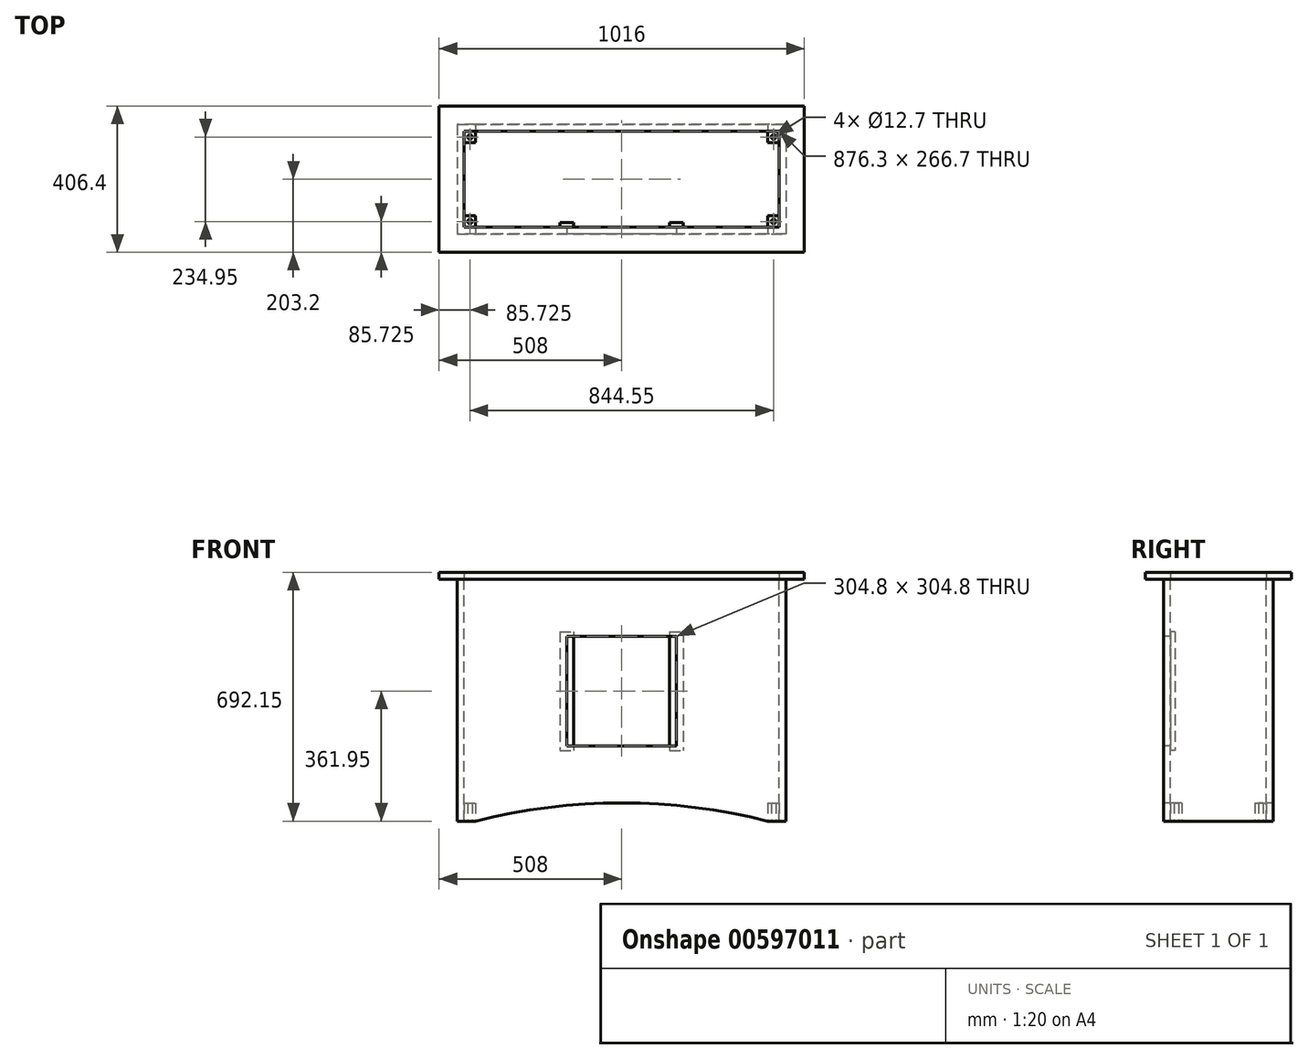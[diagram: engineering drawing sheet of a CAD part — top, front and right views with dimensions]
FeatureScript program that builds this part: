
annotation { "Feature Type Name" : "Feature", "Feature Type Description" : "" }
export const myFeature = defineFeature(function(context is Context, id is Id, definition is map)
    precondition{}
    {
        {
            var Q0;
            Q0=qCreatedBy(makeId("Front.planeOp"),FACE);
            var sketch = newSketch(context, id + "F0", { "sketchPlane" : qUnion([Q0])});
            skLineSegment(sketch, "E0", {"start": v(-406.4, -336.55) * mm, "end": v(-457.2, -336.55) * mm});
            skLineSegment(sketch, "E1", {"start": v(-457.2, -336.55) * mm, "end": v(-457.2, 336.55) * mm});
            skLineSegment(sketch, "E2", {"start": v(-457.2, 336.55) * mm, "end": v(457.2, 336.55) * mm});
            skLineSegment(sketch, "E3", {"start": v(457.2, 336.55) * mm, "end": v(457.2, -336.55) * mm});
            skLineSegment(sketch, "E4", {"start": v(457.2, -336.55) * mm, "end": v(406.4, -336.55) * mm});
            skLineSegment(sketch, "E5", {"start": v(0, 336.55) * mm, "end": v(0, -336.55) * mm, "construction": true});
            skArc(sketch, "E6", {"start": v(406.4, -336.55) * mm, "mid": v(0, -285.75) * mm, "end": v(-406.4, -336.55) * mm});
            skSolve(sketch);
        }
        {
            var Q0;
            Q0 = qSketchRegion(id + "F0", true);
            extrude(context, id + "F1", {"entities" : qUnion([Q0]), "oppositeDirection" : true, "depth" : 304.8 * mm, "offsetDistance" : 25.4 * mm});
        }
        {
            var Q0;
            Q0=makeQuery(id+"F1.opExtrude","SWEPT_FACE",FACE,{"disambiguationData":[OSD([sQuery(id+"F0.wireOp",EDGE,"E2")])]});
            var sketch = newSketch(context, id + "F2", { "sketchPlane" : qUnion([Q0])});
            skLineSegment(sketch, "E7.0", {"start": v(-438.15, 19.05) * mm, "end": v(438.15, 19.05) * mm});
            skLineSegment(sketch, "E7.1", {"start": v(-438.15, 285.75) * mm, "end": v(-438.15, 19.05) * mm});
            skLineSegment(sketch, "E7.2", {"start": v(438.15, 285.75) * mm, "end": v(-438.15, 285.75) * mm});
            skLineSegment(sketch, "E7.3", {"start": v(438.15, 19.05) * mm, "end": v(438.15, 285.75) * mm});
            skSolve(sketch);
        }
        {
            var Q0;
            Q0 = qSketchRegion(id + "F2", true);
            extrude(context, id + "F3", {"entities" : qUnion([Q0]), "operationType" : NewBodyOperationType.REMOVE, "endBound" : BoundingType.THROUGH_ALL, "oppositeDirection" : true, "depth" : 25.4 * mm, "offsetDistance" : 25.4 * mm});
        }
        {
            var Q0;
            Q0=makeQuery(id+"F1.opExtrude","CAP_FACE",FACE,{"disambiguationData":[OSD([sQuery(id+"F0.wireOp",EDGE,"E0"),sQuery(id+"F0.wireOp",EDGE,"E1"),sQuery(id+"F0.wireOp",EDGE,"E2"),sQuery(id+"F0.wireOp",EDGE,"E3"),sQuery(id+"F0.wireOp",EDGE,"E4"),sQuery(id+"F0.wireOp",EDGE,"E6")])],"isStart":true});
            var sketch = newSketch(context, id + "F4", { "sketchPlane" : qUnion([Q0])});
            skLineSegment(sketch, "E8", {"start": v(0, 336.55) * mm, "end": v(0, -285.75) * mm});
            skLineSegment(sketch, "E9.bottom", {"start": v(152.4, 177.8) * mm, "end": v(-152.4, 177.8) * mm});
            skLineSegment(sketch, "E9.top", {"start": v(152.4, -127) * mm, "end": v(-152.4, -127) * mm});
            skLineSegment(sketch, "E9.left", {"start": v(152.4, 177.8) * mm, "end": v(152.4, -127) * mm});
            skLineSegment(sketch, "E9.right", {"start": v(-152.4, 177.8) * mm, "end": v(-152.4, -127) * mm});
            skPoint(sketch, "E9.middle", {"position": v(0, 25.4) * mm});
            skSolve(sketch);
        }
        {
            var Q0;
            Q0 = qSketchRegion(id + "F4", true);
            extrude(context, id + "F5", {"entities" : qUnion([Q0]), "operationType" : NewBodyOperationType.REMOVE, "oppositeDirection" : true, "depth" : 25.4 * mm, "offsetDistance" : 25.4 * mm});
        }
        {
            var Q0;
            Q0=makeQuery(id+"F3.boolean.opBoolean","COPY",FACE,{"derivedFrom":makeQuery(id+"F3.opExtrude","SWEPT_FACE",FACE,{"disambiguationData":[OSD([sQuery(id+"F2.wireOp",EDGE,"E7.0")])]})});
            var sketch = newSketch(context, id + "F6", { "sketchPlane" : qUnion([Q0])});
            skLineSegment(sketch, "E10.bottom", {"start": v(171.25, 190.5) * mm, "end": v(133.15, 190.5) * mm});
            skLineSegment(sketch, "E10.top", {"start": v(171.25, -139.7) * mm, "end": v(133.15, -139.7) * mm});
            skLineSegment(sketch, "E10.left", {"start": v(171.25, 190.5) * mm, "end": v(171.25, -139.7) * mm});
            skLineSegment(sketch, "E10.right", {"start": v(133.15, 190.5) * mm, "end": v(133.15, -139.7) * mm});
            skLineSegment(sketch, "E11.bottom", {"start": v(-133.35, 190.5) * mm, "end": v(-171.45, 190.5) * mm});
            skLineSegment(sketch, "E11.top", {"start": v(-133.35, -139.7) * mm, "end": v(-171.45, -139.7) * mm});
            skLineSegment(sketch, "E11.left", {"start": v(-133.35, 190.5) * mm, "end": v(-133.35, -139.7) * mm});
            skLineSegment(sketch, "E11.right", {"start": v(-171.45, 190.5) * mm, "end": v(-171.45, -139.7) * mm});
            skSolve(sketch);
        }
        {
            var Q0;
            Q0 = qSketchRegion(id + "F6", true);
            extrude(context, id + "F7", {"entities" : qUnion([Q0]), "depth" : 12.7 * mm, "offsetDistance" : 25.4 * mm});
        }
        {
            var Q0;
            Q0=makeQuery(id+"F1.opExtrude","SWEPT_FACE",FACE,{"disambiguationData":[OSD([sQuery(id+"F0.wireOp",EDGE,"E2")])]});
            var sketch = newSketch(context, id + "F8", { "sketchPlane" : qUnion([Q0])});
            skLineSegment(sketch, "E12.bottom", {"start": v(-508, 355.6) * mm, "end": v(508, 355.6) * mm});
            skLineSegment(sketch, "E12.top", {"start": v(-508, -50.8) * mm, "end": v(508, -50.8) * mm});
            skLineSegment(sketch, "E12.left", {"start": v(-508, 355.6) * mm, "end": v(-508, -50.8) * mm});
            skLineSegment(sketch, "E12.right", {"start": v(508, 355.6) * mm, "end": v(508, -50.8) * mm});
            skPoint(sketch, "E12.middle", {"position": v(0, 152.4) * mm});
            skPoint(sketch, "E12.middle.positionSnap0", {"position": v(-438.15, 152.4) * mm});
            skPoint(sketch, "E12.middle.positionSnap1", {"position": v(0, 285.75) * mm});
            skPoint(sketch, "E12.centerSnap0", {"position": v(-438.15, 152.4) * mm});
            skPoint(sketch, "E12.centerSnap1", {"position": v(0, 285.75) * mm});
            skLineSegment(sketch, "E13.0", {"start": v(-438.15, 285.75) * mm, "end": v(-438.15, 19.05) * mm});
            skLineSegment(sketch, "E13.1", {"start": v(438.15, 285.75) * mm, "end": v(-438.15, 285.75) * mm});
            skLineSegment(sketch, "E13.2", {"start": v(438.15, 19.05) * mm, "end": v(438.15, 285.75) * mm});
            skLineSegment(sketch, "E13.3", {"start": v(-438.15, 19.05) * mm, "end": v(438.15, 19.05) * mm});
            skSolve(sketch);
        }
        {
            var Q0;
            Q0 = qSketchRegion(id + "F8", true);
            extrude(context, id + "F9", {"entities" : qUnion([Q0]), "depth" : 19.05 * mm, "offsetDistance" : 25.4 * mm});
        }
        {
            var Q0;
            Q0=makeQuery(id+"F1.opExtrude","SWEPT_FACE",FACE,{"disambiguationData":[OSD([sQuery(id+"F0.wireOp",EDGE,"E0")])]});
            var sketch = newSketch(context, id + "F10", { "sketchPlane" : qUnion([Q0])});
            skLineSegment(sketch, "E14.bottom", {"start": v(-438.15, -19.05) * mm, "end": v(-406.4, -19.05) * mm});
            skLineSegment(sketch, "E14.top", {"start": v(-438.15, -50.8) * mm, "end": v(-406.4, -50.8) * mm});
            skLineSegment(sketch, "E14.left", {"start": v(-438.15, -19.05) * mm, "end": v(-438.15, -50.8) * mm});
            skLineSegment(sketch, "E14.right", {"start": v(-406.4, -19.05) * mm, "end": v(-406.4, -50.8) * mm});
            skLineSegment(sketch, "E15.bottom", {"start": v(-438.15, -285.75) * mm, "end": v(-406.4, -285.75) * mm});
            skLineSegment(sketch, "E15.top", {"start": v(-438.15, -254) * mm, "end": v(-406.4, -254) * mm});
            skLineSegment(sketch, "E15.left", {"start": v(-438.15, -285.75) * mm, "end": v(-438.15, -254) * mm});
            skLineSegment(sketch, "E15.right", {"start": v(-406.4, -285.75) * mm, "end": v(-406.4, -254) * mm});
            skLineSegment(sketch, "E16.bottom", {"start": v(438.15, -19.05) * mm, "end": v(406.4, -19.05) * mm});
            skLineSegment(sketch, "E16.top", {"start": v(438.15, -50.8) * mm, "end": v(406.4, -50.8) * mm});
            skLineSegment(sketch, "E16.left", {"start": v(438.15, -19.05) * mm, "end": v(438.15, -50.8) * mm});
            skLineSegment(sketch, "E16.right", {"start": v(406.4, -19.05) * mm, "end": v(406.4, -50.8) * mm});
            skLineSegment(sketch, "E17.bottom", {"start": v(406.4, -254) * mm, "end": v(438.15, -254) * mm});
            skLineSegment(sketch, "E17.top", {"start": v(406.4, -285.75) * mm, "end": v(438.15, -285.75) * mm});
            skLineSegment(sketch, "E17.left", {"start": v(406.4, -254) * mm, "end": v(406.4, -285.75) * mm});
            skLineSegment(sketch, "E17.right", {"start": v(438.15, -254) * mm, "end": v(438.15, -285.75) * mm});
            skCircle(sketch, "E18", {"center": v(-422.28, -34.92) * mm, "radius": 6.35 * mm});
            skPoint(sketch, "E18.centerSnap0", {"position": v(-438.15, -34.92) * mm});
            skPoint(sketch, "E18.centerSnap1", {"position": v(-422.28, -50.8) * mm});
            skCircle(sketch, "E19", {"center": v(-422.28, -269.88) * mm, "radius": 6.35 * mm});
            skLineSegment(sketch, "E20", {"start": v(-438.15, -254) * mm, "end": v(-406.4, -285.75) * mm, "construction": true});
            skCircle(sketch, "E21", {"center": v(422.28, -269.88) * mm, "radius": 6.35 * mm});
            skPoint(sketch, "E21.centerSnap0", {"position": v(406.4, -269.88) * mm});
            skPoint(sketch, "E21.centerSnap1", {"position": v(422.28, -254) * mm});
            skCircle(sketch, "E22", {"center": v(422.28, -34.93) * mm, "radius": 6.35 * mm});
            skPoint(sketch, "E22.centerSnap0", {"position": v(406.4, -34.93) * mm});
            skPoint(sketch, "E22.centerSnap1", {"position": v(422.28, -19.05) * mm});
            skSolve(sketch);
        }
        {
            var Q0;
            Q0 = qSketchRegion(id + "F10", true);
            extrude(context, id + "F11", {"entities" : qUnion([Q0]), "oppositeDirection" : true, "depth" : 50.8 * mm, "offsetDistance" : 25.4 * mm});
        }
    });
